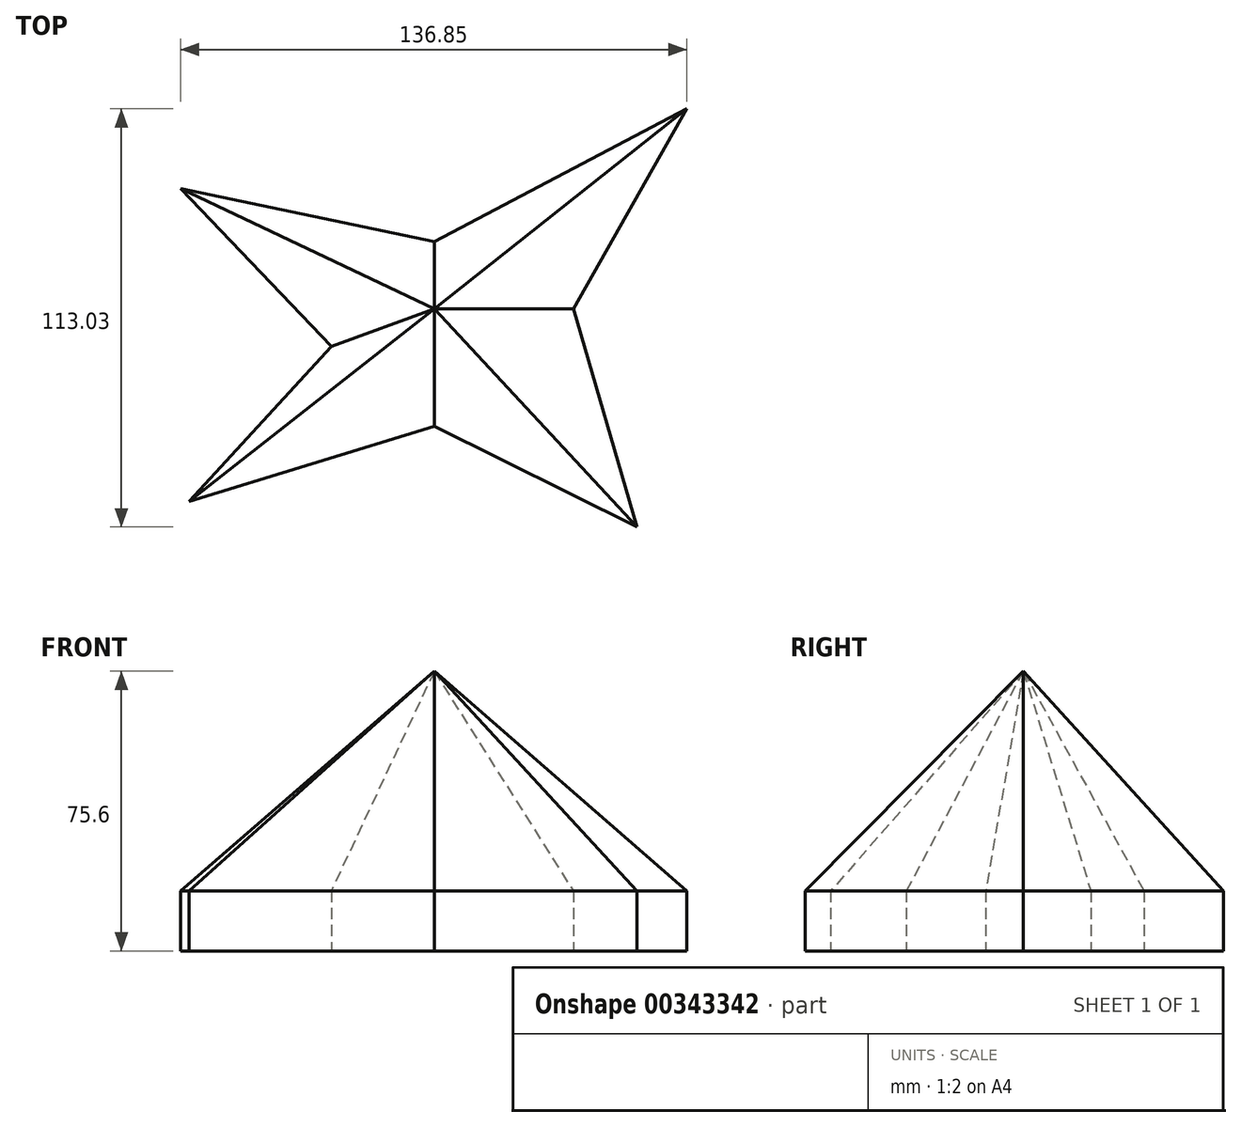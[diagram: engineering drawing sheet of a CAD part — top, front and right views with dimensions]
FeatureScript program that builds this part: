
annotation { "Feature Type Name" : "Feature", "Feature Type Description" : "" }
export const myFeature = defineFeature(function(context is Context, id is Id, definition is map)
    precondition{}
    {
        {
            var Q0;
            Q0=qCreatedBy(makeId("Top.planeOp"),FACE);
            var sketch = newSketch(context, id + "F0", { "sketchPlane" : qUnion([Q0])});
            skLineSegment(sketch, "E0", {"start": v(-68.57, 32.56) * mm, "end": v(-27.83, -10.18) * mm});
            skLineSegment(sketch, "E1", {"start": v(-27.83, -10.18) * mm, "end": v(-66.27, -52.07) * mm});
            skLineSegment(sketch, "E2", {"start": v(-66.27, -52.07) * mm, "end": v(0, -31.7) * mm});
            skLineSegment(sketch, "E3", {"start": v(0, -31.7) * mm, "end": v(54.8, -58.95) * mm});
            skLineSegment(sketch, "E4", {"start": v(54.8, -58.95) * mm, "end": v(37.58, 0) * mm});
            skLineSegment(sketch, "E5", {"start": v(37.58, 0) * mm, "end": v(68.28, 54.08) * mm});
            skLineSegment(sketch, "E6", {"start": v(68.28, 54.08) * mm, "end": v(0, 18.22) * mm});
            skLineSegment(sketch, "E7", {"start": v(0, 18.22) * mm, "end": v(-68.57, 32.56) * mm});
            skSolve(sketch);
        }
        {
            var Q0;
            Q0=makeQuery(id+"F0.imprint","IMPRINT",FACE,{"disambiguationData":[TD([[makeQuery(id+"F0.imprint","IMPRINT",EDGE,{"derivedFrom":sQuery(id+"F0.wireOp",EDGE,"E0")}),1.0]])]});
            extrude(context, id + "F1", {"entities" : qUnion([Q0]), "depth" : 16.2 * mm});
        }
        {
            var Q0;
            Q0=qCreatedBy(makeId("Top.planeOp"),FACE);
            cPlane(context, id + "F2", {"entities" : qUnion([Q0]), "cplaneType" : CPlaneType.OFFSET, "offset" : 75.6 * mm, "width" : 150 * mm, "height" : 150 * mm});
        }
        {
            var Q0;
            Q0=qCreatedBy(id+"F2.planeOp",FACE);
            var sketch = newSketch(context, id + "F3", { "sketchPlane" : qUnion([Q0])});
            skPoint(sketch, "E8", {"position": v(0, 0) * mm});
            skPoint(sketch, "E9", {"position": v(-146.6, 78.18) * mm});
            skSolve(sketch);
        }
        {
            var Q1;
            Q1=sQuery(id+"F3.wireOp",VERTEX,"E8");
            var Q2;
            Q2=makeQuery(id+"F1.opExtrude","CAP_FACE",FACE,{"disambiguationData":[OSD([sQuery(id+"F0.wireOp",EDGE,"E0"),sQuery(id+"F0.wireOp",EDGE,"E1"),sQuery(id+"F0.wireOp",EDGE,"E2"),sQuery(id+"F0.wireOp",EDGE,"E3"),sQuery(id+"F0.wireOp",EDGE,"E4"),sQuery(id+"F0.wireOp",EDGE,"E5"),sQuery(id+"F0.wireOp",EDGE,"E6"),sQuery(id+"F0.wireOp",EDGE,"E7")])],"isStart":false});
            loft(context, id + "F4", {"operationType" : NewBodyOperationType.ADD, "sheetProfilesArray" : [{ "sheetProfileEntities" : qUnion([Q1]) }, { "sheetProfileEntities" : qUnion([Q2]) }]});
        }
    });
